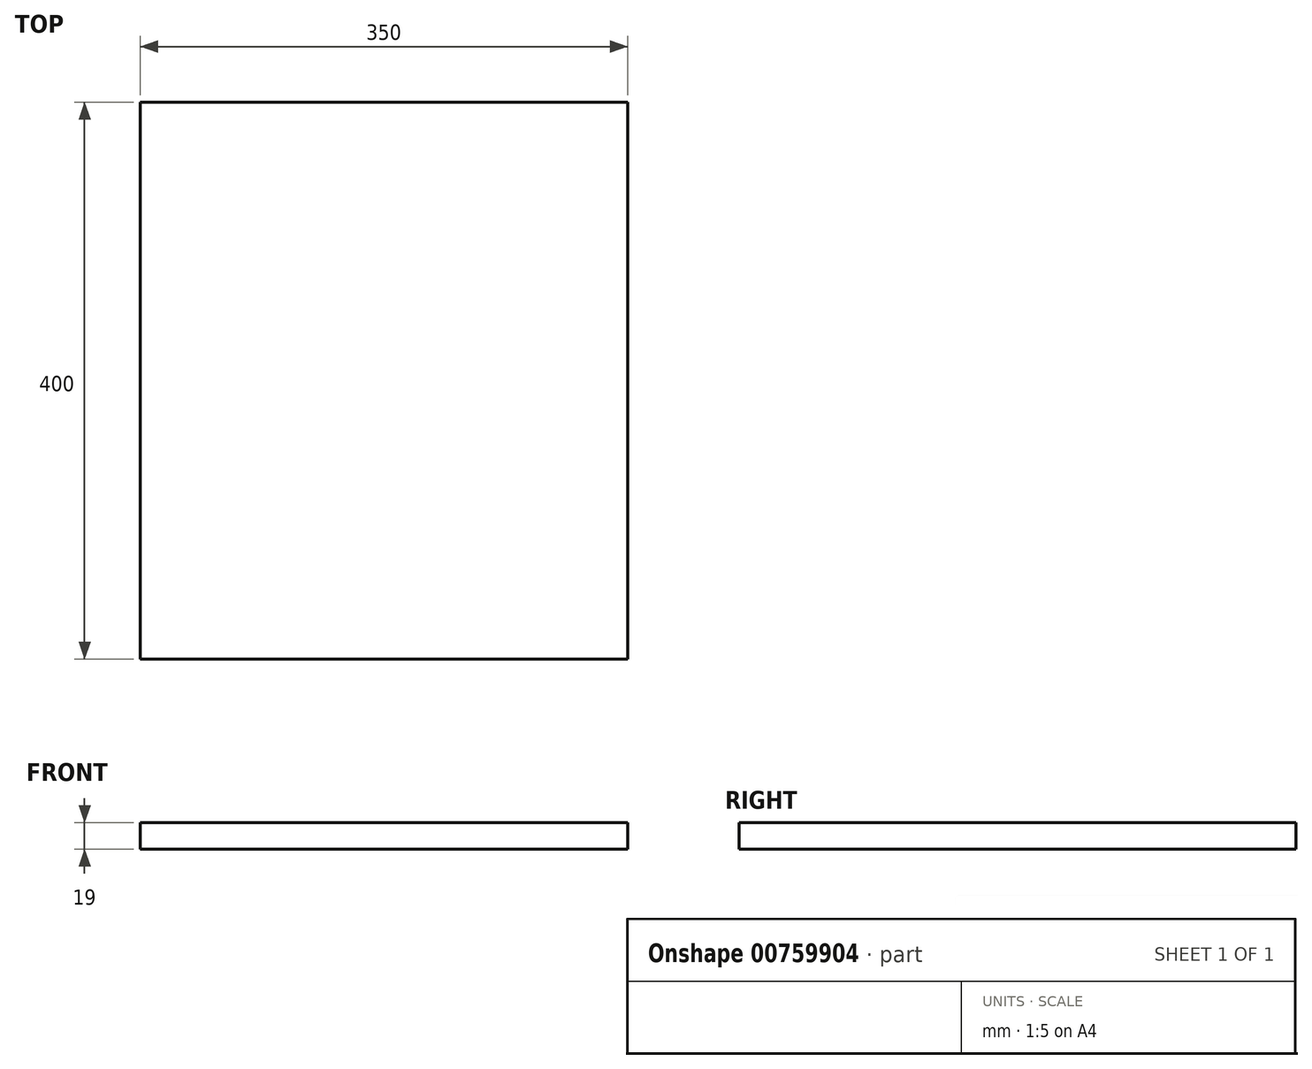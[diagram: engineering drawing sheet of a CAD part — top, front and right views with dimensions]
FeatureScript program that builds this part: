
annotation { "Feature Type Name" : "Feature", "Feature Type Description" : "" }
export const myFeature = defineFeature(function(context is Context, id is Id, definition is map)
    precondition{}
    {
        {
            var Q0;
            Q0=qCreatedBy(makeId("Top.planeOp"),FACE);
            var sketch = newSketch(context, id + "F0", { "sketchPlane" : qUnion([Q0])});
            skLineSegment(sketch, "E0.bottom", {"start": v(-110.49, -29.84) * mm, "end": v(239.51, -29.84) * mm});
            skLineSegment(sketch, "E0.top", {"start": v(-110.49, 370.16) * mm, "end": v(239.51, 370.16) * mm});
            skLineSegment(sketch, "E0.left", {"start": v(-110.49, -29.84) * mm, "end": v(-110.49, 370.16) * mm});
            skLineSegment(sketch, "E0.right", {"start": v(239.51, -29.84) * mm, "end": v(239.51, 370.16) * mm});
            skSolve(sketch);
        }
        {
            var Q0;
            Q0=makeQuery(id+"F0.imprint","IMPRINT",FACE,{"disambiguationData":[TD([[makeQuery(id+"F0.imprint","IMPRINT",EDGE,{"derivedFrom":sQuery(id+"F0.wireOp",EDGE,"E0.bottom")}),1.0]])]});
            extrude(context, id + "F1", {"entities" : qUnion([Q0]), "depth" : 19 * mm, "offsetDistance" : 25.4 * mm});
        }
    });
